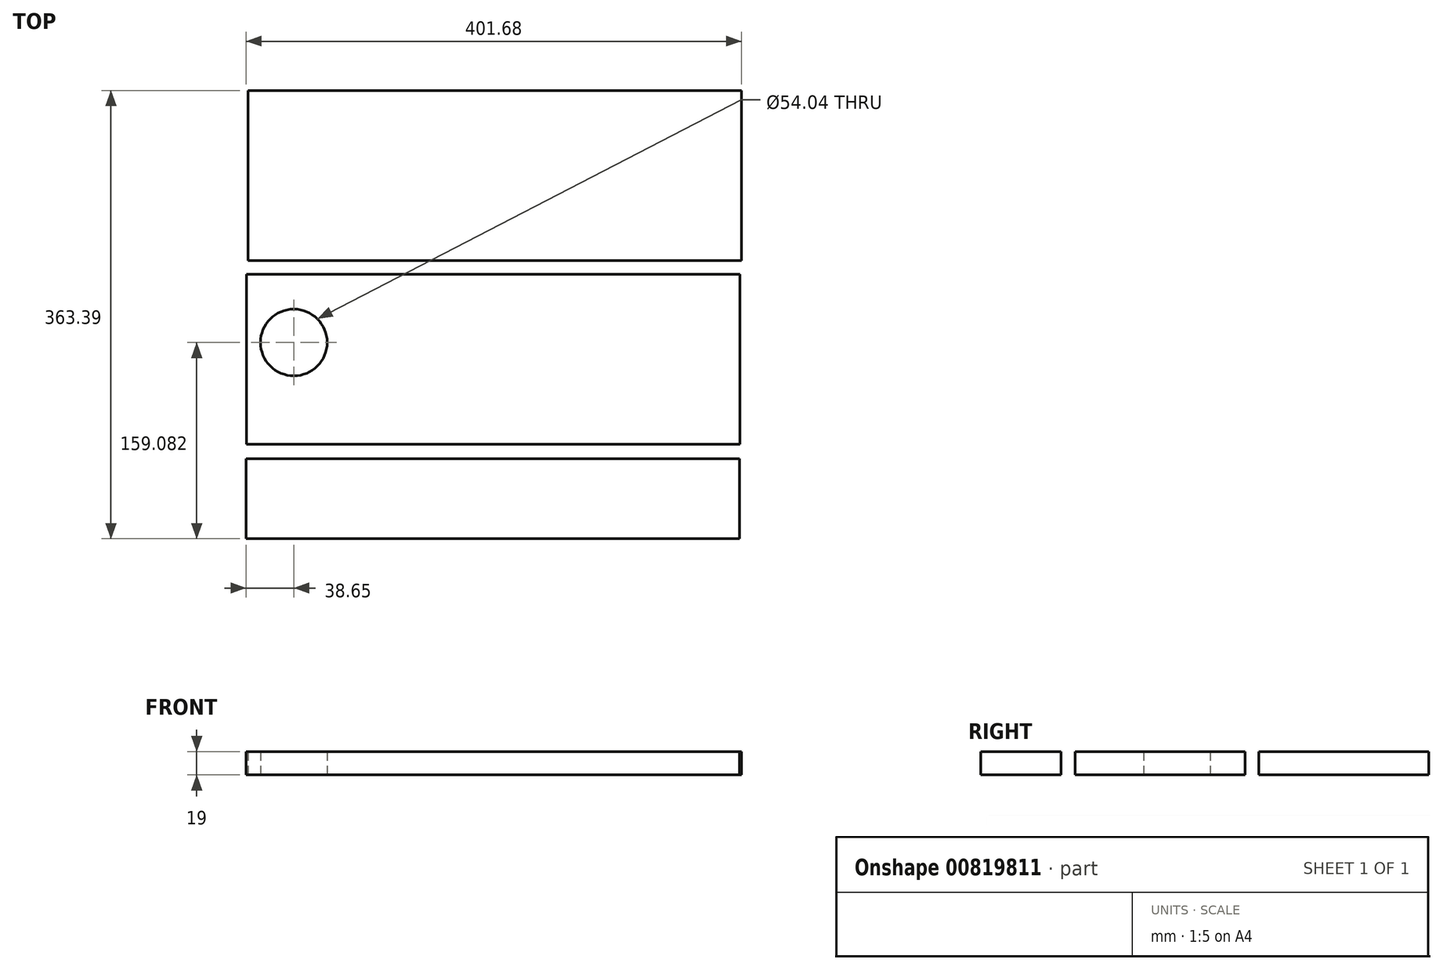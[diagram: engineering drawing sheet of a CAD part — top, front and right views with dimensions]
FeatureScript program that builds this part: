
annotation { "Feature Type Name" : "Feature", "Feature Type Description" : "" }
export const myFeature = defineFeature(function(context is Context, id is Id, definition is map)
    precondition{}
    {
        {
            var Q0;
            Q0=qCreatedBy(makeId("Top.planeOp"),FACE);
            var sketch = newSketch(context, id + "F0", { "sketchPlane" : qUnion([Q0])});
            skLineSegment(sketch, "E0.bottom", {"start": v(-327.88, 174.97) * mm, "end": v(72.12, 174.97) * mm});
            skLineSegment(sketch, "E0.top", {"start": v(-327.88, 36.97) * mm, "end": v(72.12, 36.97) * mm});
            skLineSegment(sketch, "E0.left", {"start": v(-327.88, 174.97) * mm, "end": v(-327.88, 36.97) * mm});
            skLineSegment(sketch, "E0.right", {"start": v(72.12, 174.97) * mm, "end": v(72.12, 36.97) * mm});
            skLineSegment(sketch, "E1.bottom", {"start": v(-329.31, 26.07) * mm, "end": v(70.69, 26.07) * mm});
            skLineSegment(sketch, "E1.top", {"start": v(-329.31, -111.93) * mm, "end": v(70.69, -111.93) * mm});
            skLineSegment(sketch, "E1.left", {"start": v(-329.31, 26.07) * mm, "end": v(-329.31, -111.93) * mm});
            skLineSegment(sketch, "E1.right", {"start": v(70.69, 26.07) * mm, "end": v(70.69, -111.93) * mm});
            skLineSegment(sketch, "E2.bottom", {"start": v(-329.56, -123.42) * mm, "end": v(70.44, -123.42) * mm});
            skLineSegment(sketch, "E2.top", {"start": v(-329.56, -188.42) * mm, "end": v(70.44, -188.42) * mm});
            skLineSegment(sketch, "E2.left", {"start": v(-329.56, -123.42) * mm, "end": v(-329.56, -188.42) * mm});
            skLineSegment(sketch, "E2.right", {"start": v(70.44, -123.42) * mm, "end": v(70.44, -188.42) * mm});
            skCircle(sketch, "E3", {"center": v(-290.9, -29.34) * mm, "radius": 27.02 * mm});
            skSolve(sketch);
        }
        {
            var Q0;
            Q0=makeQuery(id+"F0.imprint","IMPRINT",FACE,{"disambiguationData":[TD([[makeQuery(id+"F0.imprint","IMPRINT",EDGE,{"derivedFrom":sQuery(id+"F0.wireOp",EDGE,"E0.bottom")}),-1.0]])]});
            var Q1;
            Q1=makeQuery(id+"F0.imprint","IMPRINT",FACE,{"disambiguationData":[TD([[makeQuery(id+"F0.imprint","IMPRINT",EDGE,{"derivedFrom":sQuery(id+"F0.wireOp",EDGE,"E1.bottom")}),-1.0]])]});
            var Q2;
            Q2=makeQuery(id+"F0.imprint","IMPRINT",FACE,{"disambiguationData":[TD([[makeQuery(id+"F0.imprint","IMPRINT",EDGE,{"derivedFrom":sQuery(id+"F0.wireOp",EDGE,"E2.bottom")}),-1.0]])]});
            extrude(context, id + "F1", {"entities" : qUnion([Q0, Q1, Q2]), "depth" : 19 * mm, "offsetDistance" : 25 * mm});
        }
    });
